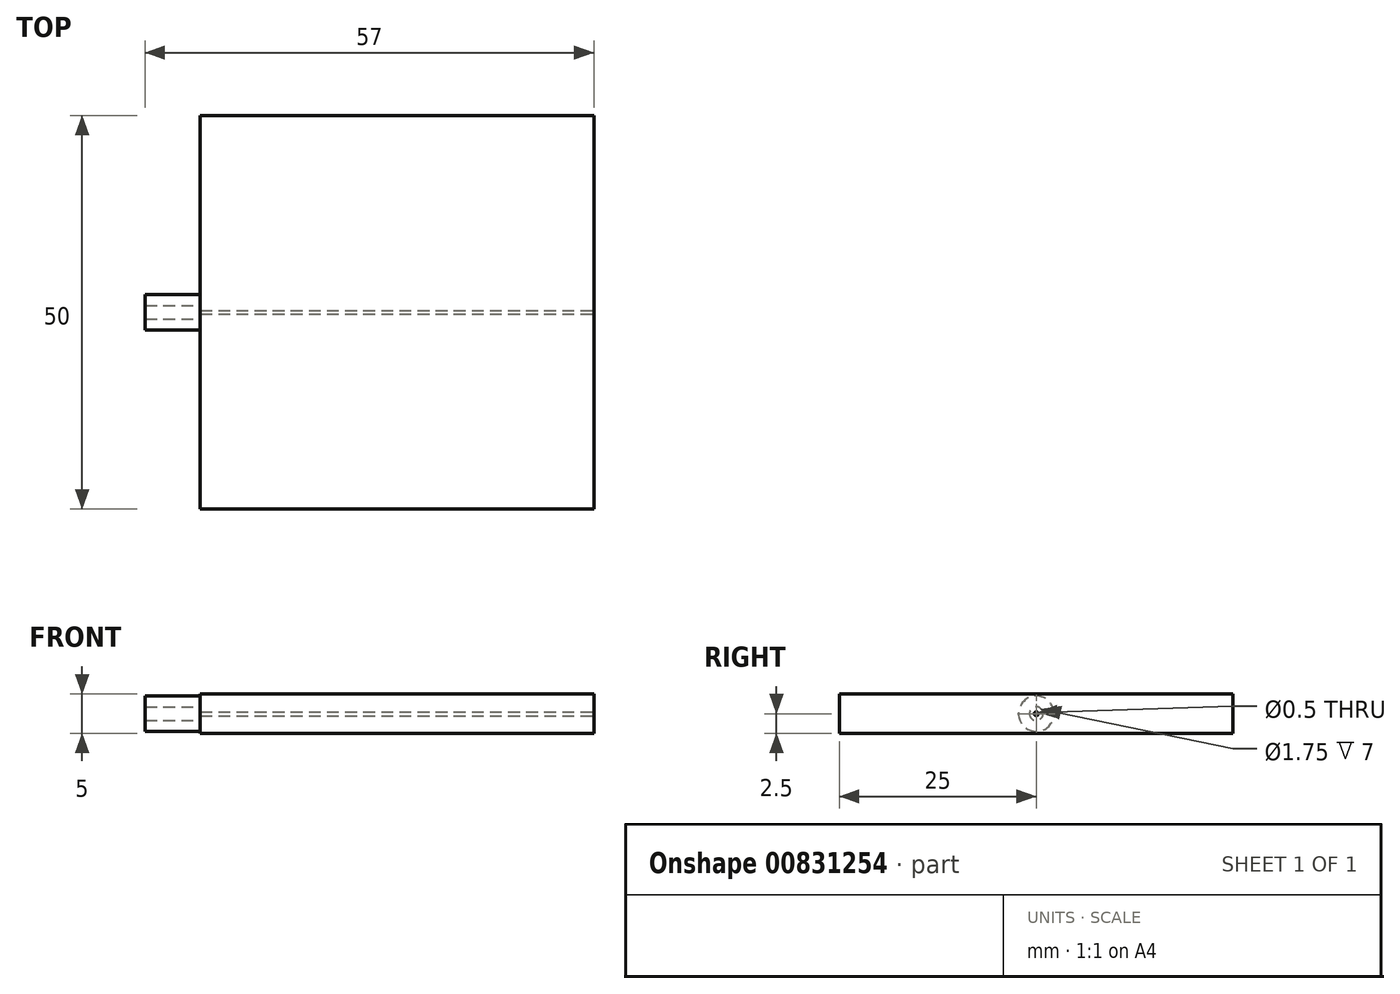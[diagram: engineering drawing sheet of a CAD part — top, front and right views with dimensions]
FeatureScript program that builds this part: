
annotation { "Feature Type Name" : "Feature", "Feature Type Description" : "" }
export const myFeature = defineFeature(function(context is Context, id is Id, definition is map)
    precondition{}
    {
        {
            var Q0;
            Q0=qCreatedBy(makeId("Top.planeOp"),FACE);
            var sketch = newSketch(context, id + "F0", { "sketchPlane" : qUnion([Q0])});
            skLineSegment(sketch, "E0", {"start": v(0, 0) * mm, "end": v(0, 50) * mm});
            skLineSegment(sketch, "E1", {"start": v(0, 50) * mm, "end": v(50, 50) * mm});
            skLineSegment(sketch, "E2", {"start": v(50, 50) * mm, "end": v(50, 0) * mm});
            skLineSegment(sketch, "E3", {"start": v(50, 0) * mm, "end": v(0, 0) * mm});
            skSolve(sketch);
        }
        {
            var Q0;
            Q0=makeQuery(id+"F0.imprint","IMPRINT",FACE,{"disambiguationData":[TD([[makeQuery(id+"F0.imprint","IMPRINT",EDGE,{"derivedFrom":sQuery(id+"F0.wireOp",EDGE,"E0")}),-1.0]])]});
            extrude(context, id + "F1", {"entities" : qUnion([Q0]), "depth" : 5 * mm, "offsetDistance" : 25 * mm});
        }
        {
            var Q0;
            Q0=makeQuery(id+"F1.opExtrude","SWEPT_FACE",FACE,{"disambiguationData":[OSD([sQuery(id+"F0.wireOp",EDGE,"E2")])]});
            var sketch = newSketch(context, id + "F2", { "sketchPlane" : qUnion([Q0])});
            skLineSegment(sketch, "E4", {"start": v(25, 5) * mm, "end": v(25, -7.91) * mm, "construction": true});
            skLineSegment(sketch, "E5", {"start": v(0, 2.5) * mm, "end": v(53.13, 2.5) * mm, "construction": true});
            skCircle(sketch, "E6", {"center": v(25, 2.5) * mm, "radius": 0.25 * mm});
            skSolve(sketch);
        }
        {
            var Q0;
            Q0=makeQuery(id+"F2.imprint","IMPRINT",FACE,{"disambiguationData":[TD([[makeQuery(id+"F2.imprint","IMPRINT",EDGE,{"derivedFrom":sQuery(id+"F2.wireOp",EDGE,"E6")}),1.0]])]});
            var Q1;
            Q1=sQuery(id+"F2.wireOp",EDGE,"E6");
            extrude(context, id + "F3", {"entities" : qUnion([Q0]), "operationType" : NewBodyOperationType.REMOVE, "surfaceEntities" : qUnion([Q1]), "oppositeDirection" : true, "depth" : 55.8 * mm, "offsetDistance" : 25 * mm});
        }
        {
            var Q0;
            Q0=makeQuery(id+"F1.opExtrude","SWEPT_FACE",FACE,{"disambiguationData":[OSD([sQuery(id+"F0.wireOp",EDGE,"E0")])]});
            var sketch = newSketch(context, id + "F4", { "sketchPlane" : qUnion([Q0])});
            skCircle(sketch, "E7", {"center": v(-25, 2.5) * mm, "radius": 0.88 * mm});
            skCircle(sketch, "E8", {"center": v(-25, 2.5) * mm, "radius": 2.25 * mm});
            skSolve(sketch);
        }
        {
            var Q0;
            Q0=makeQuery(id+"F4.imprint","IMPRINT",FACE,{"disambiguationData":[TD([[makeQuery(id+"F4.imprint","IMPRINT",EDGE,{"derivedFrom":sQuery(id+"F4.wireOp",EDGE,"E7")}),-1.0]])]});
            extrude(context, id + "F5", {"entities" : qUnion([Q0]), "operationType" : NewBodyOperationType.ADD, "depth" : 7 * mm, "offsetDistance" : 25 * mm});
        }
    });
